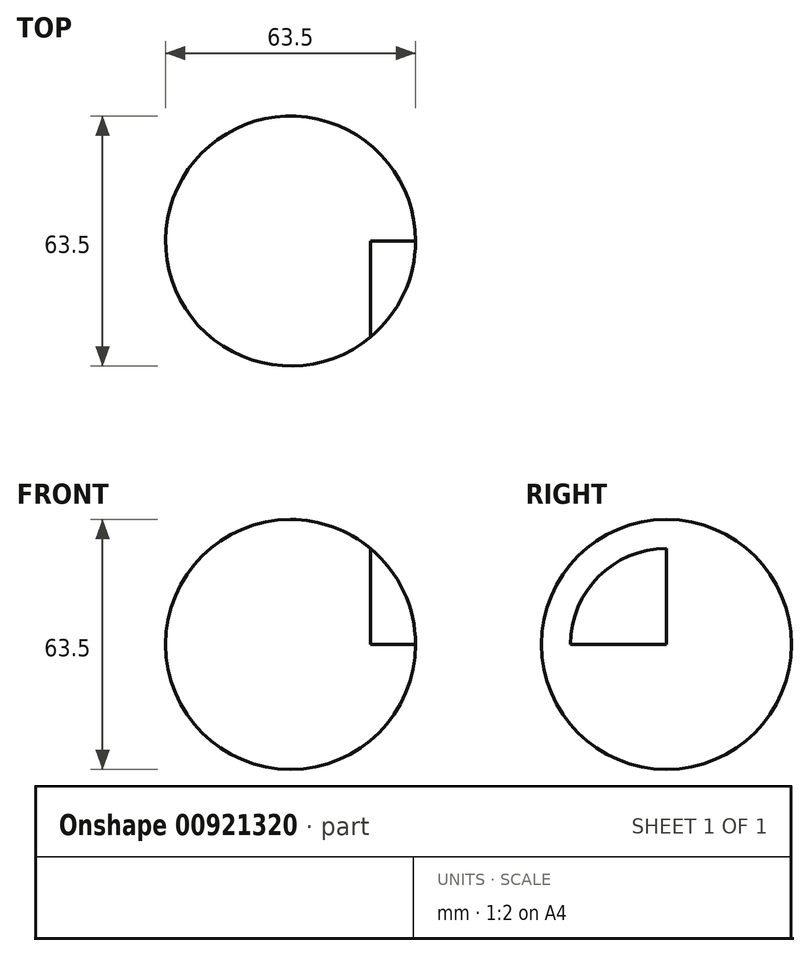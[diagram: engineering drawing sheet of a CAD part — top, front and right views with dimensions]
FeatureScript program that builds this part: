
annotation { "Feature Type Name" : "Feature", "Feature Type Description" : "" }
export const myFeature = defineFeature(function(context is Context, id is Id, definition is map)
    precondition{}
    {
        {
            var Q0;
            Q0=qCreatedBy(makeId("Front.planeOp"),FACE);
            var sketch = newSketch(context, id + "F0", { "sketchPlane" : qUnion([Q0])});
            skCircle(sketch, "E0", {"center": v(0, 0) * mm, "radius": 31.75 * mm});
            skLineSegment(sketch, "E1", {"start": v(0, 77.12) * mm, "end": v(0, -83.67) * mm});
            skLineSegment(sketch, "E2.bottom", {"start": v(20.32, 0) * mm, "end": v(58.42, 0) * mm});
            skLineSegment(sketch, "E2.top", {"start": v(20.32, 76.2) * mm, "end": v(58.42, 76.2) * mm});
            skLineSegment(sketch, "E2.left", {"start": v(20.32, 0) * mm, "end": v(20.32, 76.2) * mm});
            skLineSegment(sketch, "E2.right", {"start": v(58.42, 0) * mm, "end": v(58.42, 76.2) * mm});
            skSolve(sketch);
        }
        {
            var Q0;
            {var subQ0=sQuery(id+"F0.wireOp",EDGE,"E1");var subQ1=sQuery(id+"F0.wireOp",EDGE,"E0");var subQ2=makeQuery(id+"F0.imprint","INTERSECT",VERTEX,{"disambiguationData":[OD(0.0)],"derivedFrom":[subQ1,subQ0]});Q0=makeQuery(id+"F0.imprint","IMPRINT",FACE,{"disambiguationData":[TD([[makeQuery(id+"F0.imprint","IMPRINT",EDGE,{"disambiguationData":[TD([[subQ2,-1.0]])],"derivedFrom":subQ1}),1.0]])]});}
            var Q1;
            Q1=sQuery(id+"F0.wireOp",EDGE,"E1");
            revolve(context, id + "F1", {"surfaceOperationType" : NewSurfaceOperationType.NEW, "entities" : qUnion([Q0]), "axis" : qUnion([Q1]), "revolveType" : RevolveType.FULL});
        }
        {
            var Q0;
            Q0=makeQuery(id+"F0.imprint","IMPRINT",FACE,{"disambiguationData":[TD([[makeQuery(id+"F0.imprint","IMPRINT",EDGE,{"derivedFrom":sQuery(id+"F0.wireOp",EDGE,"E2.bottom")}),1.0]])]});
            extrude(context, id + "F2", {"entities" : qUnion([Q0]), "depth" : 25.4 * mm, "offsetDistance" : 25.4 * mm});
        }
        {
            var Q0;
            Q0=makeQuery(id+"F2.opExtrude","SWEPT_BODY",BODY,{"disambiguationData":[OSD([sQuery(id+"F0.wireOp",EDGE,"E0"),sQuery(id+"F0.wireOp",EDGE,"E2.bottom"),sQuery(id+"F0.wireOp",EDGE,"E2.left")])]});
            var Q1;
            Q1=makeQuery(id+"F1.opRevolve","SWEPT_BODY",BODY,{"disambiguationData":[OSD([sQuery(id+"F0.wireOp",EDGE,"E0"),sQuery(id+"F0.wireOp",EDGE,"E1")])]});
            var Q2;
            Q2=makeQuery(id+"F2.opExtrude","CAP_FACE",FACE,{"disambiguationData":[OSD([sQuery(id+"F0.wireOp",EDGE,"E0"),sQuery(id+"F0.wireOp",EDGE,"E2.bottom"),sQuery(id+"F0.wireOp",EDGE,"E2.left")])],"isStart":false});
            booleanBodies(context, id + "F3", {"operationType" : BooleanOperationType.SUBTRACTION, "tools" : qUnion([Q0]), "targets" : qUnion([Q1]), "offset" : true, "entitiesToOffset" : qUnion([Q2]), "offsetDistance" : 2.54 * mm});
        }
    });
